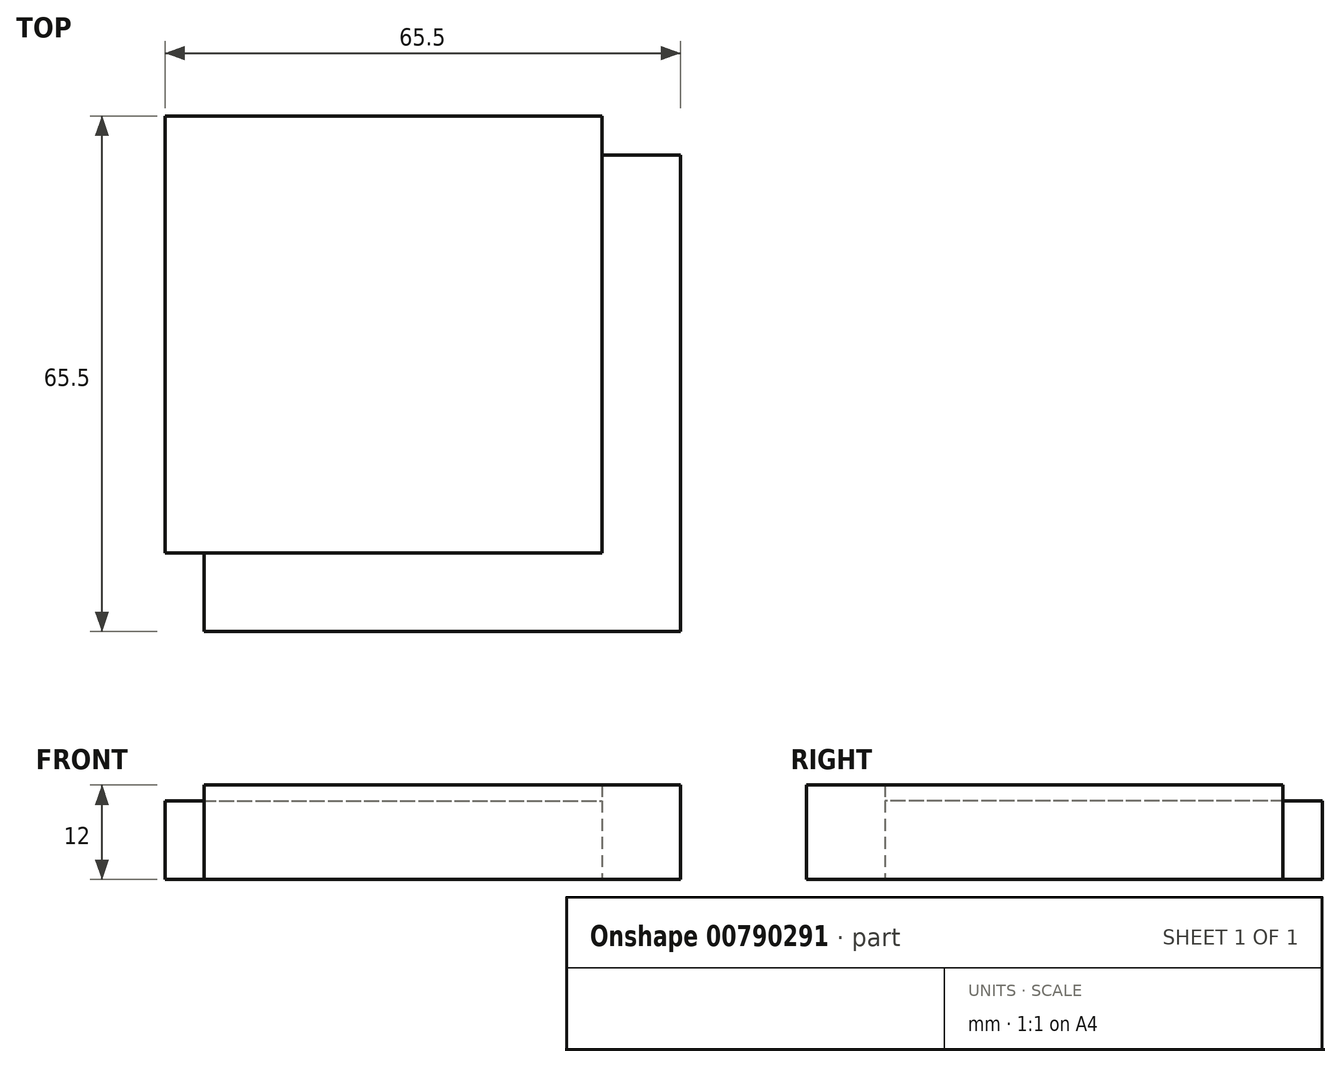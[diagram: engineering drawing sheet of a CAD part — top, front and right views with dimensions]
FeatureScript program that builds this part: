
annotation { "Feature Type Name" : "Feature", "Feature Type Description" : "" }
export const myFeature = defineFeature(function(context is Context, id is Id, definition is map)
    precondition{}
    {
        {
            var Q0;
            Q0=qCreatedBy(makeId("Top.planeOp"),FACE);
            var sketch = newSketch(context, id + "F0", { "sketchPlane" : qUnion([Q0])});
            skLineSegment(sketch, "E0.bottom", {"start": v(-90.75, 30.25) * mm, "end": v(-90.75, -30.25) * mm});
            skLineSegment(sketch, "E0.top", {"start": v(-30.25, 30.25) * mm, "end": v(-30.25, -30.25) * mm});
            skLineSegment(sketch, "E0.left", {"start": v(-90.75, 30.25) * mm, "end": v(-30.25, 30.25) * mm});
            skLineSegment(sketch, "E0.right", {"start": v(-90.75, -30.25) * mm, "end": v(-30.25, -30.25) * mm});
            skPoint(sketch, "E0.middle", {"position": v(-60.5, 0) * mm});
            skLineSegment(sketch, "E1.0", {"start": v(-95.75, -20.25) * mm, "end": v(-57.75, -20.25) * mm});
            skLineSegment(sketch, "E2.0", {"start": v(-40.25, 35.25) * mm, "end": v(-40.25, -2.5) * mm});
            skLineSegment(sketch, "E3.0", {"start": v(-95.75, 35.25) * mm, "end": v(-95.75, -20.25) * mm});
            skLineSegment(sketch, "E4", {"start": v(-40.25, -20.25) * mm, "end": v(-57.75, -20.25) * mm});
            skLineSegment(sketch, "E5", {"start": v(-40.25, -2.5) * mm, "end": v(-40.25, -20.25) * mm});
            skLineSegment(sketch, "E6.0", {"start": v(-95.75, 35.25) * mm, "end": v(-40.25, 35.25) * mm});
            skSolve(sketch);
        }
        {
            var Q0;
            {var subQ2=sQuery(id+"F0.wireOp",EDGE,"E0.top");Q0=makeQuery(id+"F0.imprint","IMPRINT",FACE,{"disambiguationData":[TD([[makeQuery(id+"F0.imprint","IMPRINT",EDGE,{"derivedFrom":subQ2}),-1.0]])]});}
            extrude(context, id + "F1", {"entities" : qUnion([Q0]), "depth" : 12 * mm, "offsetDistance" : 25 * mm});
        }
        {
            var Q0;
            {var subQ1=sQuery(id+"F0.wireOp",EDGE,"E1.0");Q0=makeQuery(id+"F0.imprint","IMPRINT",FACE,{"disambiguationData":[TD([[makeQuery(id+"F0.imprint","IMPRINT",EDGE,{"derivedFrom":subQ1}),1.0]])]});}
            extrude(context, id + "F2", {"entities" : qUnion([Q0]), "operationType" : NewBodyOperationType.ADD, "depth" : 10 * mm, "offsetDistance" : 25 * mm});
        }
    });
